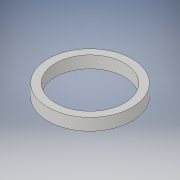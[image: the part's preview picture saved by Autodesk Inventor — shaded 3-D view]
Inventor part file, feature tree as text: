
AUTODESK INVENTOR PART (.ipt)
format: ipt  version: 2017 (Build 210142000, 142)  size: 99,328 bytes
history: native  units: mm
features: extrude x1, sketch x1
ambient origin geometry x8: Origin, YZ Plane, XZ Plane, XY Plane, X Axis, Y Axis, Z Axis, Center Point
bodies: Solid1 (feature_tree)
feature tree (2):
  extrude  "Extrusion1"  Depth=4.0mm
  sketch  "Sketch1"  dims[d0=28.0mm d1=23.0mm d2=4.0mm d3=0.0mm]
